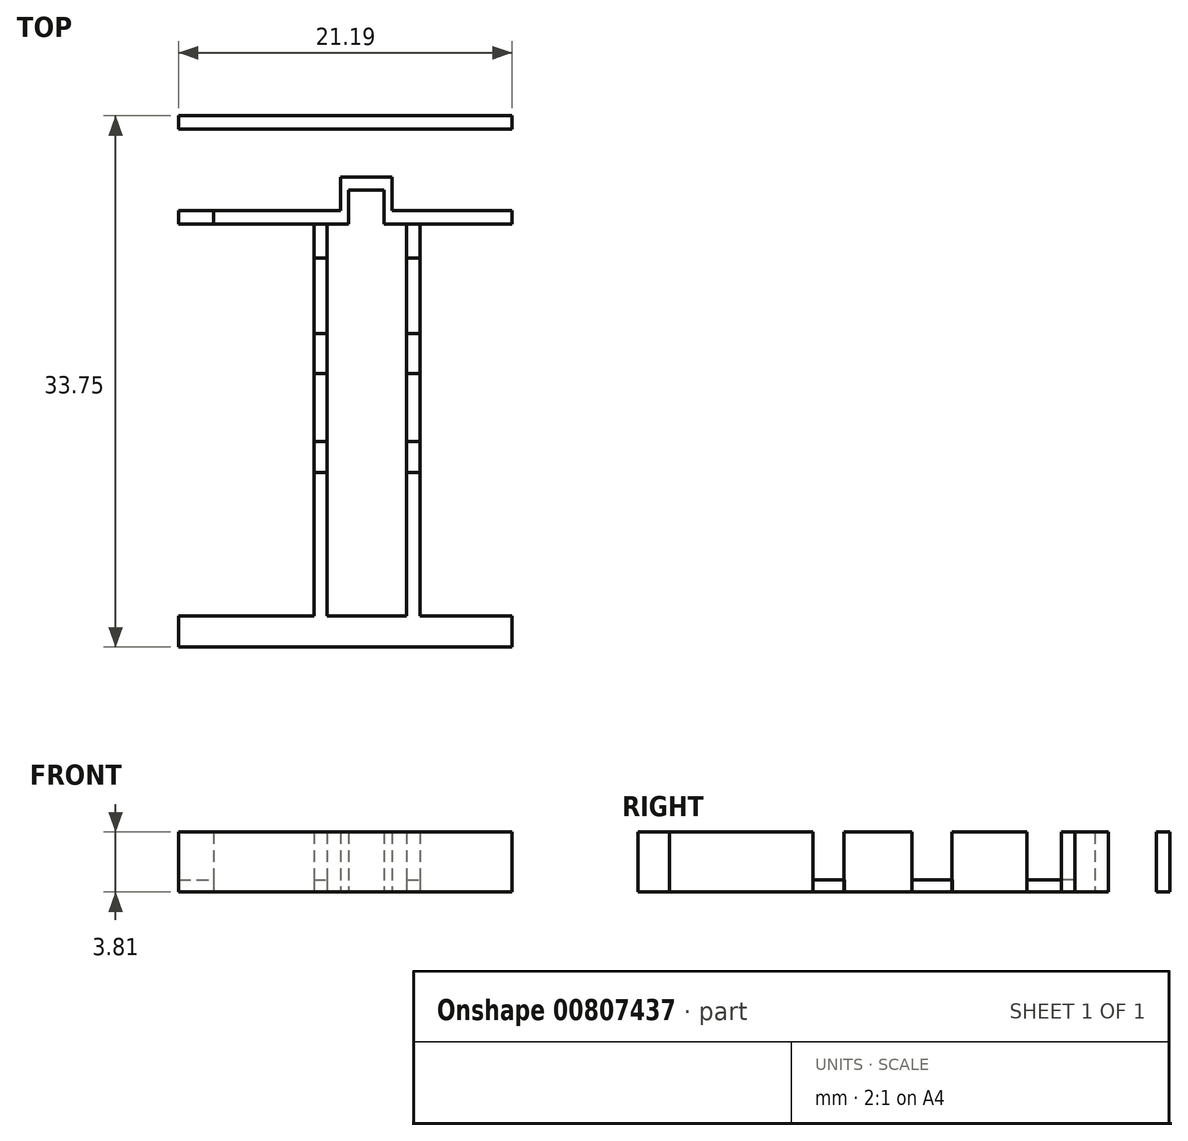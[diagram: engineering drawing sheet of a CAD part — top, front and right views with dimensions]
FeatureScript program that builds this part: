
annotation { "Feature Type Name" : "Feature", "Feature Type Description" : "" }
export const myFeature = defineFeature(function(context is Context, id is Id, definition is map)
    precondition{}
    {
        {
            var Q0;
            Q0=qCreatedBy(makeId("Top.planeOp"),FACE);
            var sketch = newSketch(context, id + "F0", { "sketchPlane" : qUnion([Q0])});
            skLineSegment(sketch, "E0.bottom", {"start": v(-25.2, -76.16) * mm, "end": v(-24.36, -76.16) * mm});
            skLineSegment(sketch, "E0.top", {"start": v(-25.2, -65.11) * mm, "end": v(-24.36, -65.11) * mm});
            skLineSegment(sketch, "E0.left", {"start": v(-25.2, -76.16) * mm, "end": v(-25.2, -65.11) * mm});
            skLineSegment(sketch, "E0.right", {"start": v(-24.36, -76.16) * mm, "end": v(-24.36, -65.11) * mm});
            skLineSegment(sketch, "E1.bottom", {"start": v(-19.3, -65.11) * mm, "end": v(-18.47, -65.11) * mm});
            skLineSegment(sketch, "E1.top", {"start": v(-19.3, -76.16) * mm, "end": v(-18.47, -76.16) * mm});
            skLineSegment(sketch, "E1.left", {"start": v(-19.3, -65.11) * mm, "end": v(-19.3, -76.16) * mm});
            skLineSegment(sketch, "E1.right", {"start": v(-18.47, -65.11) * mm, "end": v(-18.47, -76.16) * mm});
            skLineSegment(sketch, "E2.bottom", {"start": v(-25.2, -58.81) * mm, "end": v(-24.36, -58.81) * mm});
            skLineSegment(sketch, "E2.top", {"start": v(-25.2, -63.13) * mm, "end": v(-24.36, -63.13) * mm});
            skLineSegment(sketch, "E2.left", {"start": v(-25.2, -58.81) * mm, "end": v(-25.2, -63.13) * mm});
            skLineSegment(sketch, "E2.right", {"start": v(-24.36, -58.81) * mm, "end": v(-24.36, -63.13) * mm});
            skLineSegment(sketch, "E3.bottom", {"start": v(-18.47, -63.13) * mm, "end": v(-19.3, -63.13) * mm});
            skLineSegment(sketch, "E3.top", {"start": v(-18.47, -58.81) * mm, "end": v(-19.3, -58.81) * mm});
            skLineSegment(sketch, "E3.left", {"start": v(-18.47, -63.13) * mm, "end": v(-18.47, -58.81) * mm});
            skLineSegment(sketch, "E3.right", {"start": v(-19.3, -63.13) * mm, "end": v(-19.3, -58.81) * mm});
            skLineSegment(sketch, "E4.bottom", {"start": v(-24.36, -51.5) * mm, "end": v(-25.2, -51.5) * mm});
            skLineSegment(sketch, "E4.top", {"start": v(-24.36, -56.27) * mm, "end": v(-25.2, -56.27) * mm});
            skLineSegment(sketch, "E4.left", {"start": v(-24.36, -51.5) * mm, "end": v(-24.36, -56.27) * mm});
            skLineSegment(sketch, "E4.right", {"start": v(-25.2, -51.5) * mm, "end": v(-25.2, -56.27) * mm});
            skLineSegment(sketch, "E5.bottom", {"start": v(-19.3, -51.5) * mm, "end": v(-18.47, -51.5) * mm});
            skLineSegment(sketch, "E5.top", {"start": v(-19.3, -56.27) * mm, "end": v(-18.47, -56.27) * mm});
            skLineSegment(sketch, "E5.left", {"start": v(-19.3, -51.5) * mm, "end": v(-19.3, -56.27) * mm});
            skLineSegment(sketch, "E5.right", {"start": v(-18.47, -51.5) * mm, "end": v(-18.47, -56.27) * mm});
            skLineSegment(sketch, "E6.bottom", {"start": v(-23, -49.31) * mm, "end": v(-31.56, -49.31) * mm});
            skLineSegment(sketch, "E6.top", {"start": v(-23, -48.48) * mm, "end": v(-31.56, -48.48) * mm});
            skLineSegment(sketch, "E6.left", {"start": v(-23, -49.31) * mm, "end": v(-23, -48.48) * mm});
            skLineSegment(sketch, "E6.right", {"start": v(-31.56, -49.31) * mm, "end": v(-31.56, -48.48) * mm});
            skLineSegment(sketch, "E7.bottom", {"start": v(-12.6, -49.31) * mm, "end": v(-20.74, -49.31) * mm});
            skLineSegment(sketch, "E7.top", {"start": v(-12.6, -48.48) * mm, "end": v(-20.74, -48.48) * mm});
            skLineSegment(sketch, "E7.left", {"start": v(-12.6, -49.31) * mm, "end": v(-12.6, -48.48) * mm});
            skLineSegment(sketch, "E7.right", {"start": v(-20.74, -49.31) * mm, "end": v(-20.74, -48.48) * mm});
            skLineSegment(sketch, "E8.bottom", {"start": v(-12.6, -43.28) * mm, "end": v(-33.79, -43.28) * mm});
            skLineSegment(sketch, "E8.top", {"start": v(-12.6, -42.45) * mm, "end": v(-33.79, -42.45) * mm});
            skLineSegment(sketch, "E8.left", {"start": v(-12.6, -43.28) * mm, "end": v(-12.6, -42.45) * mm});
            skLineSegment(sketch, "E8.right", {"start": v(-33.79, -43.28) * mm, "end": v(-33.79, -42.45) * mm});
            skLineSegment(sketch, "E9.bottom", {"start": v(-33.86, -43.28) * mm, "end": v(-33.79, -43.28) * mm});
            skLineSegment(sketch, "E10.bottom", {"start": v(-23, -48.48) * mm, "end": v(-23.5, -48.48) * mm});
            skLineSegment(sketch, "E10.top", {"start": v(-23, -46.33) * mm, "end": v(-23.5, -46.33) * mm});
            skLineSegment(sketch, "E10.left", {"start": v(-23, -48.48) * mm, "end": v(-23, -46.33) * mm});
            skLineSegment(sketch, "E10.right", {"start": v(-23.5, -48.48) * mm, "end": v(-23.5, -46.33) * mm});
            skLineSegment(sketch, "E11.bottom", {"start": v(-20.74, -48.48) * mm, "end": v(-20.23, -48.48) * mm});
            skLineSegment(sketch, "E11.top", {"start": v(-20.74, -46.34) * mm, "end": v(-20.23, -46.34) * mm});
            skLineSegment(sketch, "E11.left", {"start": v(-20.74, -48.48) * mm, "end": v(-20.74, -46.34) * mm});
            skLineSegment(sketch, "E11.right", {"start": v(-20.23, -48.48) * mm, "end": v(-20.23, -46.34) * mm});
            skLineSegment(sketch, "E12.bottom", {"start": v(-20.74, -46.34) * mm, "end": v(-23, -46.34) * mm});
            skLineSegment(sketch, "E12.top", {"start": v(-20.74, -47.18) * mm, "end": v(-23, -47.18) * mm});
            skLineSegment(sketch, "E12.left", {"start": v(-20.74, -46.34) * mm, "end": v(-20.74, -47.18) * mm});
            skLineSegment(sketch, "E12.right", {"start": v(-23, -46.34) * mm, "end": v(-23, -47.18) * mm});
            skLineSegment(sketch, "E13.bottom", {"start": v(-33.79, -76.2) * mm, "end": v(-12.6, -76.2) * mm});
            skLineSegment(sketch, "E13.top", {"start": v(-33.79, -74.22) * mm, "end": v(-12.6, -74.22) * mm});
            skLineSegment(sketch, "E13.left", {"start": v(-33.79, -76.2) * mm, "end": v(-33.79, -74.22) * mm});
            skLineSegment(sketch, "E13.right", {"start": v(-12.6, -76.2) * mm, "end": v(-12.6, -74.22) * mm});
            skSolve(sketch);
        }
        {
            var Q0;
            Q0 = qSketchRegion(id + "F0", true);
            extrude(context, id + "F1", {"entities" : qUnion([Q0]), "depth" : 3.8 * mm, "offsetDistance" : 25.4 * mm});
        }
        {
            var Q0;
            Q0=qCreatedBy(makeId("Top.planeOp"),FACE);
            var sketch = newSketch(context, id + "F2", { "sketchPlane" : qUnion([Q0])});
            skLineSegment(sketch, "E14.bottom", {"start": v(-33.79, -48.48) * mm, "end": v(-31.56, -48.48) * mm});
            skLineSegment(sketch, "E14.top", {"start": v(-33.79, -49.31) * mm, "end": v(-31.56, -49.31) * mm});
            skLineSegment(sketch, "E14.left", {"start": v(-33.79, -48.48) * mm, "end": v(-33.79, -49.31) * mm});
            skLineSegment(sketch, "E14.right", {"start": v(-31.56, -48.48) * mm, "end": v(-31.56, -49.31) * mm});
            skLineSegment(sketch, "E15.bottom", {"start": v(-25.2, -49.29) * mm, "end": v(-24.36, -49.29) * mm});
            skLineSegment(sketch, "E15.top", {"start": v(-25.2, -51.5) * mm, "end": v(-24.36, -51.5) * mm});
            skLineSegment(sketch, "E15.left", {"start": v(-25.2, -49.29) * mm, "end": v(-25.2, -51.5) * mm});
            skLineSegment(sketch, "E15.right", {"start": v(-24.36, -49.29) * mm, "end": v(-24.36, -51.5) * mm});
            skLineSegment(sketch, "E16.bottom", {"start": v(-19.3, -49.29) * mm, "end": v(-18.47, -49.29) * mm});
            skLineSegment(sketch, "E16.top", {"start": v(-19.3, -51.5) * mm, "end": v(-18.47, -51.5) * mm});
            skLineSegment(sketch, "E16.left", {"start": v(-19.3, -49.29) * mm, "end": v(-19.3, -51.5) * mm});
            skLineSegment(sketch, "E16.right", {"start": v(-18.47, -49.29) * mm, "end": v(-18.47, -51.5) * mm});
            skLineSegment(sketch, "E17.bottom", {"start": v(-25.2, -56.25) * mm, "end": v(-24.36, -56.25) * mm});
            skLineSegment(sketch, "E17.top", {"start": v(-25.2, -58.81) * mm, "end": v(-24.36, -58.81) * mm});
            skLineSegment(sketch, "E17.left", {"start": v(-25.2, -56.25) * mm, "end": v(-25.2, -58.81) * mm});
            skLineSegment(sketch, "E17.right", {"start": v(-24.36, -56.25) * mm, "end": v(-24.36, -58.81) * mm});
            skLineSegment(sketch, "E18.bottom", {"start": v(-25.2, -63.1) * mm, "end": v(-24.36, -63.1) * mm});
            skLineSegment(sketch, "E18.top", {"start": v(-25.2, -65.11) * mm, "end": v(-24.36, -65.11) * mm});
            skLineSegment(sketch, "E18.left", {"start": v(-25.2, -63.1) * mm, "end": v(-25.2, -65.11) * mm});
            skLineSegment(sketch, "E18.right", {"start": v(-24.36, -63.1) * mm, "end": v(-24.36, -65.11) * mm});
            skLineSegment(sketch, "E19.bottom", {"start": v(-19.3, -56.25) * mm, "end": v(-18.47, -56.25) * mm});
            skLineSegment(sketch, "E19.top", {"start": v(-19.3, -58.81) * mm, "end": v(-18.47, -58.81) * mm});
            skLineSegment(sketch, "E19.left", {"start": v(-19.3, -56.25) * mm, "end": v(-19.3, -58.81) * mm});
            skLineSegment(sketch, "E19.right", {"start": v(-18.47, -56.25) * mm, "end": v(-18.47, -58.81) * mm});
            skLineSegment(sketch, "E20.bottom", {"start": v(-19.3, -63.1) * mm, "end": v(-18.47, -63.1) * mm});
            skLineSegment(sketch, "E20.top", {"start": v(-19.3, -65.11) * mm, "end": v(-18.47, -65.11) * mm});
            skLineSegment(sketch, "E20.left", {"start": v(-19.3, -63.1) * mm, "end": v(-19.3, -65.11) * mm});
            skLineSegment(sketch, "E20.right", {"start": v(-18.47, -63.1) * mm, "end": v(-18.47, -65.11) * mm});
            skSolve(sketch);
        }
        {
            var Q0;
            Q0 = qSketchRegion(id + "F2", true);
            extrude(context, id + "F3", {"entities" : qUnion([Q0]), "depth" : 0.76 * mm, "offsetDistance" : 25.4 * mm});
        }
    });
